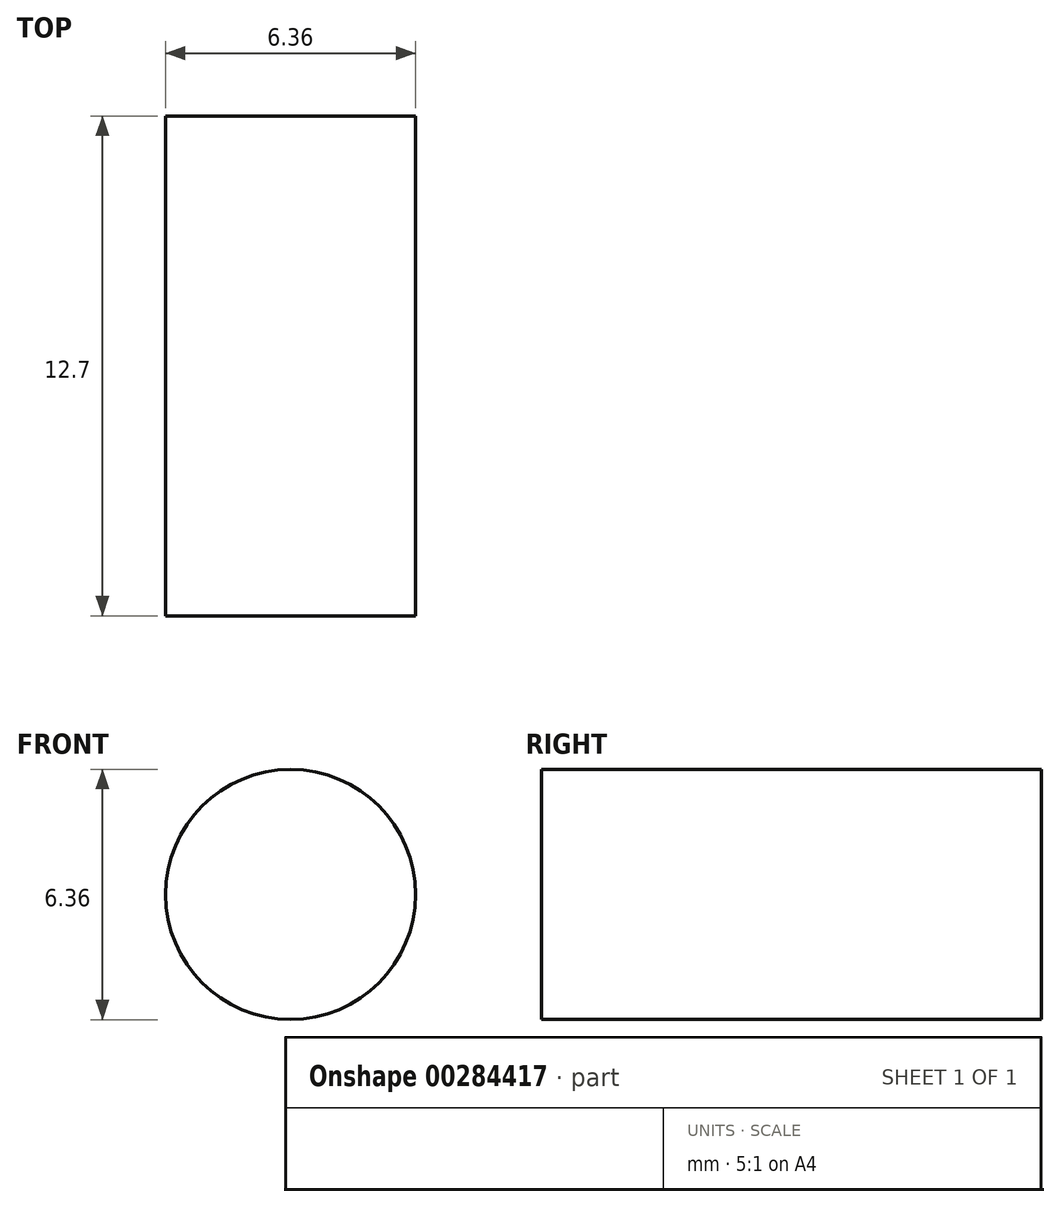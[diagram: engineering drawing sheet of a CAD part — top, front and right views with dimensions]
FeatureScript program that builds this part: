
annotation { "Feature Type Name" : "Feature", "Feature Type Description" : "" }
export const myFeature = defineFeature(function(context is Context, id is Id, definition is map)
    precondition{}
    {
        {
            var Q0;
            Q0=qCreatedBy(makeId("Front.planeOp"),FACE);
            var sketch = newSketch(context, id + "F0", { "sketchPlane" : qUnion([Q0])});
            skCircle(sketch, "E0", {"center": v(0, 0) * mm, "radius": 3.17 * mm});
            skSolve(sketch);
        }
        {
            var Q0;
            Q0 = qSketchRegion(id + "F0", true);
            extrude(context, id + "F1", {"entities" : qUnion([Q0]), "depth" : 12.7 * mm, "symmetric" : true});
        }
    });
